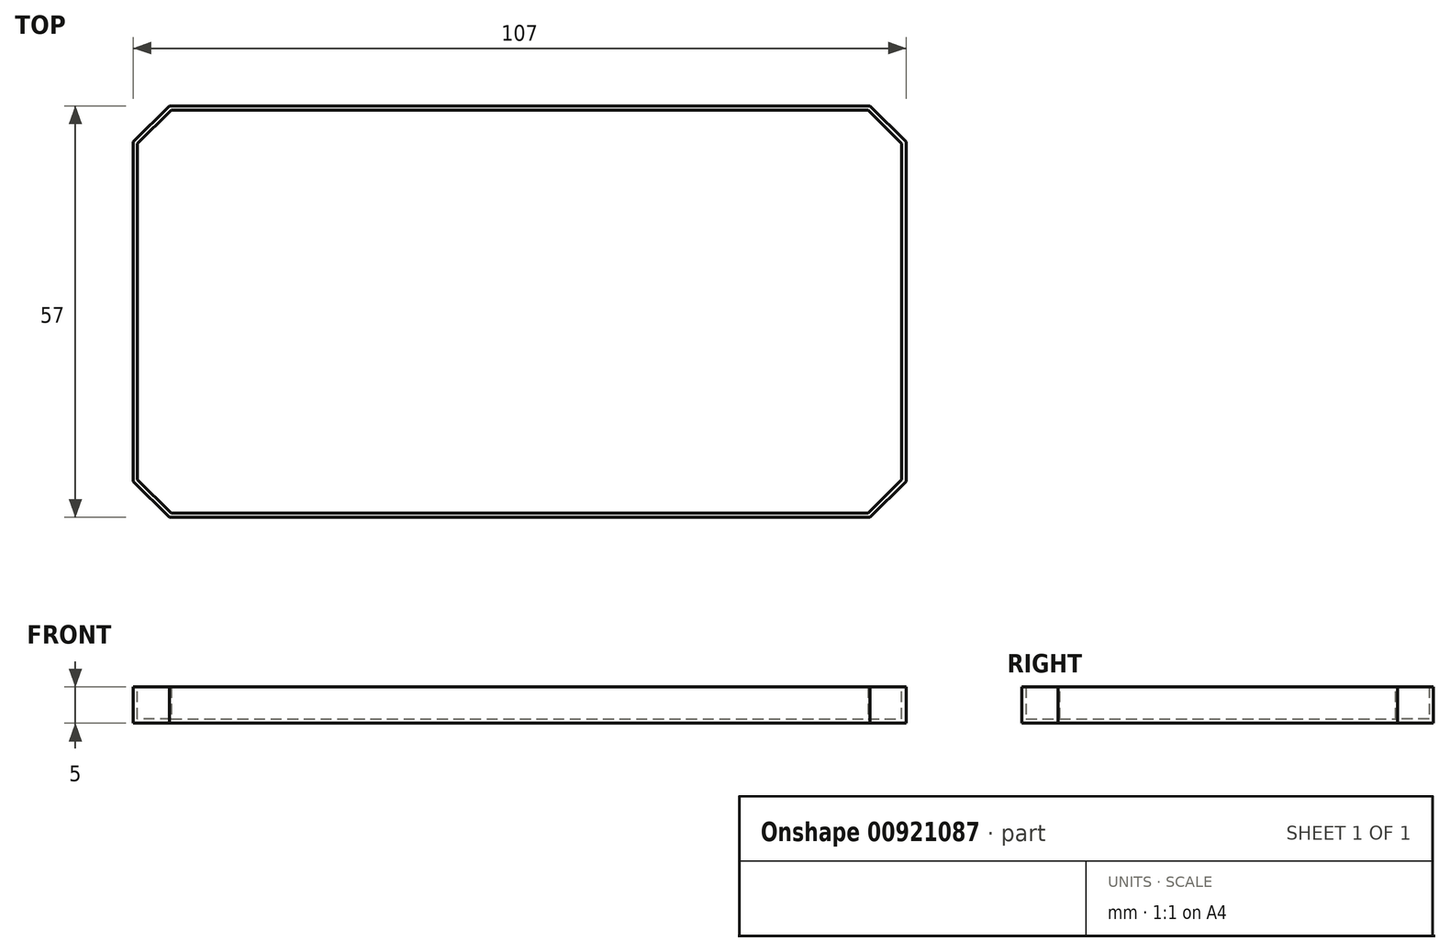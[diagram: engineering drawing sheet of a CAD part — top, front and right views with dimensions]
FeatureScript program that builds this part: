
annotation { "Feature Type Name" : "Feature", "Feature Type Description" : "" }
export const myFeature = defineFeature(function(context is Context, id is Id, definition is map)
    precondition{}
    {
        {
            var Q0;
            Q0=qCreatedBy(makeId("Top.planeOp"),FACE);
            var sketch = newSketch(context, id + "F0", { "sketchPlane" : qUnion([Q0])});
            skLineSegment(sketch, "E0.bottom", {"start": v(-1, -1) * mm, "end": v(106, -1) * mm});
            skLineSegment(sketch, "E0.top", {"start": v(-1, 56) * mm, "end": v(106, 56) * mm});
            skLineSegment(sketch, "E0.left", {"start": v(-1, -1) * mm, "end": v(-1, 56) * mm});
            skLineSegment(sketch, "E0.right", {"start": v(106, -1) * mm, "end": v(106, 56) * mm});
            skSolve(sketch);
        }
        {
            var Q0;
            Q0=makeQuery(id+"F0.imprint","IMPRINT",FACE,{"disambiguationData":[TD([[makeQuery(id+"F0.imprint","IMPRINT",EDGE,{"derivedFrom":sQuery(id+"F0.wireOp",EDGE,"E0.bottom")}),1.0]])]});
            extrude(context, id + "F1", {"entities" : qUnion([Q0]), "depth" : 5 * mm, "offsetDistance" : 25 * mm});
        }
        {
            var Q0;
            Q0=makeQuery(id+"F1.opExtrude","CAP_FACE",FACE,{"disambiguationData":[OSD([sQuery(id+"F0.wireOp",EDGE,"E0.bottom"),sQuery(id+"F0.wireOp",EDGE,"E0.top"),sQuery(id+"F0.wireOp",EDGE,"E0.left"),sQuery(id+"F0.wireOp",EDGE,"E0.right")])],"isStart":false});
            var sketch = newSketch(context, id + "F2", { "sketchPlane" : qUnion([Q0])});
            skCircle(sketch, "E1", {"center": v(19, 19) * mm, "radius": 10 * mm});
            skCircle(sketch, "E2", {"center": v(19, 54) * mm, "radius": 10 * mm});
            skCircle(sketch, "E3", {"center": v(54, 54) * mm, "radius": 10 * mm});
            skCircle(sketch, "E4", {"center": v(54, 19) * mm, "radius": 10 * mm});
            skLineSegment(sketch, "E5", {"start": v(19, 54) * mm, "end": v(293.88, 54) * mm, "construction": true});
            skPoint(sketch, "E6", {"position": v(156.44, 54) * mm});
            skLineSegment(sketch, "E7", {"start": v(19, 19) * mm, "end": v(19, 54) * mm, "construction": true});
            skLineSegment(sketch, "E8", {"start": v(54, 54) * mm, "end": v(54, 19) * mm, "construction": true});
            skLineSegment(sketch, "E9", {"start": v(19, 19) * mm, "end": v(225.78, 19) * mm, "construction": true});
            skLineSegment(sketch, "E10", {"start": v(89, 54) * mm, "end": v(89, 19) * mm, "construction": true});
            skLineSegment(sketch, "E11", {"start": v(124, 54) * mm, "end": v(124, 19) * mm, "construction": true});
            skCircle(sketch, "E12", {"center": v(89, 54) * mm, "radius": 10 * mm});
            skCircle(sketch, "E13", {"center": v(89, 19) * mm, "radius": 10 * mm});
            skCircle(sketch, "E14", {"center": v(124, 54) * mm, "radius": 10 * mm});
            skCircle(sketch, "E15", {"center": v(124, 19) * mm, "radius": 10 * mm});
            skSolve(sketch);
        }
        {
            var Q0;
            Q0=makeQuery(id+"F1.opExtrude","SWEPT_EDGE",EDGE,{"disambiguationData":[OSD([sQuery(id+"F0.wireOp",EDGE,"E0.bottom"),sQuery(id+"F0.wireOp",EDGE,"E0.left")])]});
            var Q1;
            Q1=makeQuery(id+"F1.opExtrude","SWEPT_EDGE",EDGE,{"disambiguationData":[OSD([sQuery(id+"F0.wireOp",EDGE,"E0.bottom"),sQuery(id+"F0.wireOp",EDGE,"E0.right")])]});
            var Q2;
            Q2=makeQuery(id+"F1.opExtrude","SWEPT_EDGE",EDGE,{"disambiguationData":[OSD([sQuery(id+"F0.wireOp",EDGE,"E0.top"),sQuery(id+"F0.wireOp",EDGE,"E0.right")])]});
            var Q3;
            Q3=makeQuery(id+"F1.opExtrude","SWEPT_EDGE",EDGE,{"disambiguationData":[OSD([sQuery(id+"F0.wireOp",EDGE,"E0.top"),sQuery(id+"F0.wireOp",EDGE,"E0.left")])]});
            chamfer(context, id + "F3", {"entities" : qUnion([Q0, Q1, Q2, Q3]), "width" : 5 * mm, "tangentPropagation" : true});
        }
        {
            var Q0;
            Q0=makeQuery(id+"F1.opExtrude","CAP_FACE",FACE,{"disambiguationData":[OSD([sQuery(id+"F0.wireOp",EDGE,"E0.bottom"),sQuery(id+"F0.wireOp",EDGE,"E0.top"),sQuery(id+"F0.wireOp",EDGE,"E0.left"),sQuery(id+"F0.wireOp",EDGE,"E0.right")])],"isStart":false});
            shell(context, id + "F4", {"entities" : qUnion([Q0]), "thickness" : .6 * mm});
        }
    });
